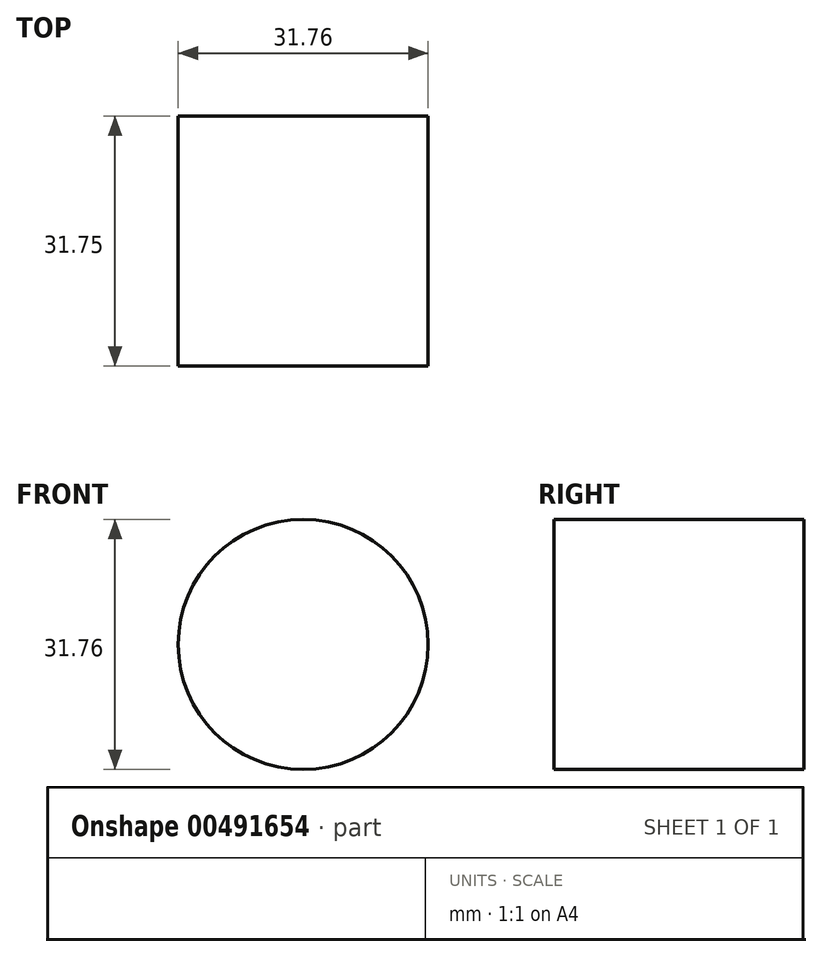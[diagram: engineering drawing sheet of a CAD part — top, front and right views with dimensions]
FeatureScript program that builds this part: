
annotation { "Feature Type Name" : "Feature", "Feature Type Description" : "" }
export const myFeature = defineFeature(function(context is Context, id is Id, definition is map)
    precondition{}
    {
        {
            var Q0;
            Q0=qCreatedBy(makeId("Front.planeOp"),FACE);
            var sketch = newSketch(context, id + "F0", { "sketchPlane" : qUnion([Q0])});
            skCircle(sketch, "E0", {"center": v(0, 0) * mm, "radius": 15.88 * mm});
            skSolve(sketch);
        }
        {
            var Q0;
            Q0=makeQuery(id+"F0.imprint","IMPRINT",FACE,{"disambiguationData":[TD([[makeQuery(id+"F0.imprint","IMPRINT",EDGE,{"derivedFrom":sQuery(id+"F0.wireOp",EDGE,"E0")}),1.0]])]});
            var Q1;
            Q1=sQuery(id+"F0.wireOp",EDGE,"E0");
            extrude(context, id + "F1", {"entities" : qUnion([Q0]), "surfaceEntities" : qUnion([Q1]), "depth" : 31.75 * mm});
        }
    });
